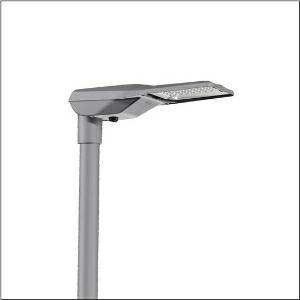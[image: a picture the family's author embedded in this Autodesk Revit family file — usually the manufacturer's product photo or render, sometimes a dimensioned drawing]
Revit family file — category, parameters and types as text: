
# Revit family: streetlight_sl_21_mini___p0_8a_5xe2u33r08hb_8bcd
name_source: partatom
category: Lighting Fixtures
units: mm (PartAtom-declared; Revit-internal decimal feet)

## family parameters
Cut with Voids When Loaded = No
Host = Face
Light Source = No
Part Type = Normal
Room Calculation Point = No
Round Connector Dimension = Use Diameter
Shared = No

## types (1)
- --- (1 x LED, 9120 lm, 66 W, 3000K)
    Apparent Load = 66 VA
    CIE Flux Codes = 33 69 96 100 100
    Color Rendering = 70
    Color Temperature = 3000K
    Default Elevation = 1800 mm
    Description = Streetlight SL 21 mini, mast luminaire, primary light control with lens, of PMMA, primary optical cover: cover, of toughened safety glass, transparent, light distribution: P0.8a, light emission: direct distribution, primary light characteristic: asymmetric, installation type: post-top, side-entry, LED, High Power LED, rated luminous flux: 9.120lm, luminous efficacy: 138lm/W, light colour: 730, colour temperature: 3000K, control gear: D4i, control: pre-setting: logarithmic dimming characteristic, flexible luminous flux parameterisation, time-dependent luminous flux control, constant luminous flux control, overheat protection, mains connection: 220..240V, AC, 50/60Hz, start of lifetime: 66W, end of service life: 69W, reduction: 30W, luminaire housing, of diecast aluminium, powder-coated, SITECO metallic grey (DB 702S), corrosivity category C5 high according to DIN EN ISO 12944, multi-level sealing system, sealing non-destructively replaceable, inclination adjustable: 0°, 5°, 10°, 15°, please order mast flange separately, length: 628mm, width: 235mm, height: 110mm, mast flange for spigot size: 42mm (side-entry): 5XC10008XM4, 60/48mm (side-entry/post-top): 5XC10108XM2, 76/60mm (side-entry/post-top): 5XC10108XM1, mounting height: 4..8m, Smart Interface below, protection rating (complete): IP66, insulation class (complete): insulation class II (safety insulation), certification: CE, ENEC, ENEC+, VDE, impact resistance: IK10, permissible operating ambient temperature for outdoor applications: -40..+50°C, standard-compliant lighting for roads and squares, packaging unit: 1 piece

Light Distribution: P0.8a
    Height = 110 mm
    Lamp = 1 x LED
    Lamp Light Flux = 9120 lm
    Lamp Power = 66 W
    Lamp count = 1
    Length = 625 mm
    Luminous efficacy = 138 lm/W
    Manufacturer = Siteco
    ModVariant = No
    Model = 5XE2U33R08HB
    Number of Poles = 1
    OnlyDefault = Yes
    Power Factor = 1
    Product Name = Streetlight SL 21 mini | P0.8a
    Product group = mast luminaire | pylon top
    ProductGroupID = 6100
    Protection Class = Protection class II
    Protection Degree = IP 66
    RLX_Detail_Level = 1
    RLX_Emergency_Light_Flux = 0 lm
    RLX_Emergency_Type = 0
    RLX_Emergency_Type_DB = No
    RlxData = <blob elided: 92049 chars, md5=4098f387>
    Socket = socket
    Standby Power = 0 W
    System Light Flux = 9120 lm
    System Power = 66 W
    Type Comments = factory setting: luminous flux: 100 % | dim-lin: 254 | 670 mA
    Type Image = l_1003516.jpg
    URL = http://relux.com
    VarID = @adj_080291
    Voltage = 0 V
    Weight = 0.00 kg
    Width = 234 mm

## geometry (parser evidence)
native form markers: Blend x4, Sweep x12
no freeform markers — native parametric forms only
